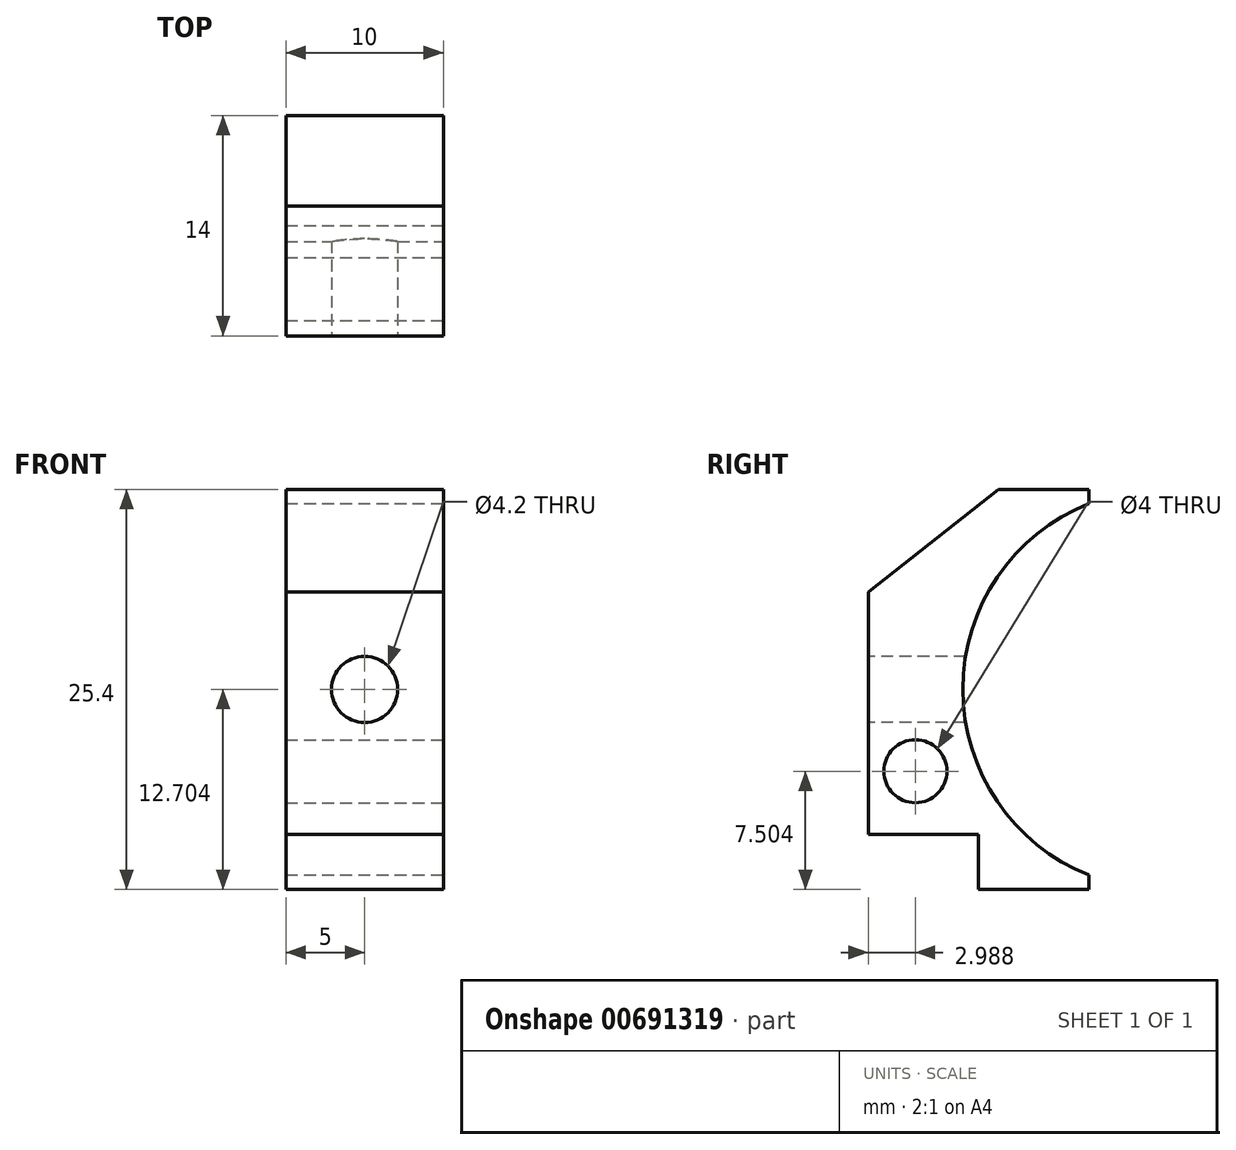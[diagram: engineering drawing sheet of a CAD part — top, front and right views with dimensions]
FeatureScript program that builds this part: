
annotation { "Feature Type Name" : "Feature", "Feature Type Description" : "" }
export const myFeature = defineFeature(function(context is Context, id is Id, definition is map)
    precondition{}
    {
        {
            var Q0;
            Q0=qCreatedBy(makeId("Front.planeOp"),FACE);
            var sketch = newSketch(context, id + "F0", { "sketchPlane" : qUnion([Q0])});
            skLineSegment(sketch, "E0.top", {"start": v(0, 21.04) * mm, "end": v(10, 21.04) * mm});
            skLineSegment(sketch, "E0.left", {"start": v(0, 0) * mm, "end": v(0, 21.04) * mm});
            skLineSegment(sketch, "E0.right", {"start": v(10, 0) * mm, "end": v(10, 21.04) * mm});
            skLineSegment(sketch, "E1.top", {"start": v(10, -4.36) * mm, "end": v(0, -4.36) * mm});
            skLineSegment(sketch, "E1.left", {"start": v(10, 0) * mm, "end": v(10, -4.36) * mm});
            skLineSegment(sketch, "E1.right", {"start": v(0, 0) * mm, "end": v(0, -4.36) * mm});
            skSolve(sketch);
        }
        {
            var Q0;
            Q0 = qSketchRegion(id + "F0", true);
            extrude(context, id + "F1", {"entities" : qUnion([Q0]), "depth" : 14 * mm, "offsetDistance" : 25.4 * mm});
        }
        {
            var Q0;
            Q0=makeQuery(id+"F1.opExtrude","SWEPT_FACE",FACE,{"disambiguationData":[OSD([sQuery(id+"F0.wireOp",EDGE,"E0.right")])]});
            var sketch = newSketch(context, id + "F2", { "sketchPlane" : qUnion([Q0])});
            skLineSegment(sketch, "E2", {"start": v(1.53, 21.04) * mm, "end": v(24.73, 21.04) * mm, "construction": true});
            skLineSegment(sketch, "E3.bottom", {"start": v(1.53, 21.04) * mm, "end": v(7.88, 21.04) * mm});
            skLineSegment(sketch, "E3.top", {"start": v(2.6, -4.36) * mm, "end": v(8.96, -4.36) * mm});
            skPoint(sketch, "E4.centerSnap0", {"position": v(1.53, 8.34) * mm});
            skPoint(sketch, "E4.centerSnap1", {"position": v(4.7, 21.04) * mm});
            skLineSegment(sketch, "E5", {"start": v(0, -4.36) * mm, "end": v(0, 21.04) * mm});
            skPoint(sketch, "E6", {"position": v(7.88, 8.34) * mm});
            skLineSegment(sketch, "E7", {"start": v(-14, 8.34) * mm, "end": v(-8.02, 8.34) * mm, "construction": true});
            skLineSegment(sketch, "E8", {"start": v(4.7, 21.04) * mm, "end": v(4.7, 8.34) * mm});
            skLineSegment(sketch, "E9", {"start": v(1.53, 8.34) * mm, "end": v(7.88, 8.34) * mm, "construction": true});
            skLineSegment(sketch, "E10.bottom", {"start": v(1.53, 21.04) * mm, "end": v(7.87, 21.04) * mm});
            skLineSegment(sketch, "E10.top", {"start": v(1.53, -4.36) * mm, "end": v(7.87, -4.36) * mm});
            skLineSegment(sketch, "E10.left", {"start": v(1.53, 21.04) * mm, "end": v(1.53, -4.36) * mm});
            skLineSegment(sketch, "E10.right", {"start": v(7.87, 21.04) * mm, "end": v(7.87, -4.36) * mm});
            skPoint(sketch, "E10.middle", {"position": v(4.7, 8.34) * mm});
            skArc(sketch, "E11", {"start": v(1.52, 21.04) * mm, "mid": v(-2.07, 19.55) * mm, "end": v(-5.07, 17.06) * mm, "construction": true});
            skLineSegment(sketch, "E12", {"start": v(4.7, 8.34) * mm, "end": v(0, 20.56) * mm, "construction": true});
            skLineSegment(sketch, "E13", {"start": v(4.7, 8.34) * mm, "end": v(1.52, 21.04) * mm, "construction": true});
            skArc(sketch, "E14", {"start": v(4.7, 21.04) * mm, "mid": v(-8, 8.34) * mm, "end": v(4.7, -4.36) * mm});
            skLineSegment(sketch, "E15", {"start": v(-7, -4.36) * mm, "end": v(0, -4.36) * mm});
            skLineSegment(sketch, "E16", {"start": v(-7, -4.36) * mm, "end": v(-7, -0.86) * mm});
            skLineSegment(sketch, "E17", {"start": v(-7, -0.86) * mm, "end": v(-14, -0.86) * mm});
            skLineSegment(sketch, "E18", {"start": v(-14, -0.86) * mm, "end": v(-14, 8.34) * mm});
            skLineSegment(sketch, "E19", {"start": v(-38, -0.86) * mm, "end": v(-14, -0.86) * mm, "construction": true});
            skLineSegment(sketch, "E20", {"start": v(-34.79, -0.86) * mm, "end": v(-34.79, 3.14) * mm, "construction": true});
            skPoint(sketch, "E21.centerSnap0", {"position": v(-11.01, 8.34) * mm});
            skCircle(sketch, "E22", {"center": v(-11.01, 3.14) * mm, "radius": 2 * mm});
            skSolve(sketch);
        }
        {
            var Q0;
            {var subQ0=sQuery(id+"F2.wireOp",EDGE,"E5");var subQ3=sQuery(id+"F2.wireOp",EDGE,"THwo0RVz-D03a-z8GB-oCDg-kRwS6JTPJZCc");var subQ5=makeQuery(id+"F2.imprint","INTERSECT",VERTEX,{"derivedFrom":[subQ0,subQ3]});Q0=makeQuery(id+"F2.imprint","IMPRINT",FACE,{"disambiguationData":[TD([[makeQuery(id+"F2.imprint","IMPRINT",EDGE,{"disambiguationData":[TD([[subQ5,1.0]])],"derivedFrom":subQ3}),1.0]])]});}
            var Q1;
            {var subQ2=sQuery(id+"F2.wireOp",EDGE,"pF1QTI6O-Y2cm-lT8T-25oJ-yhtP9O5BMF4k");Q1=makeQuery(id+"F2.imprint","IMPRINT",FACE,{"disambiguationData":[TD([[makeQuery(id+"F2.imprint","IMPRINT",EDGE,{"derivedFrom":subQ2}),-1.0]])]});}
            var Q2;
            {var subQ0=sQuery(id+"F2.wireOp",EDGE,"E5");var subQ3=sQuery(id+"F2.wireOp",EDGE,"E14");var subQ5=makeQuery(id+"F2.imprint","INTERSECT",VERTEX,{"derivedFrom":[subQ0,subQ3]});Q2=makeQuery(id+"F2.imprint","IMPRINT",FACE,{"disambiguationData":[TD([[makeQuery(id+"F2.imprint","IMPRINT",EDGE,{"disambiguationData":[TD([[subQ5,1.0]])],"derivedFrom":subQ3}),1.0]])]});}
            var Q3;
            {var subQ0=sQuery(id+"F2.wireOp",EDGE,"7ex8zuft-uerx-yqms-d6Cl-iXTFEyRzaDfW.bottom");var subQ3=sQuery(id+"F2.wireOp",EDGE,"E14");var subQ4=makeQuery(id+"F2.imprint","INTERSECT",VERTEX,{"derivedFrom":[subQ0,subQ3]});Q3=makeQuery(id+"F2.imprint","IMPRINT",FACE,{"disambiguationData":[TD([[makeQuery(id+"F2.imprint","IMPRINT",EDGE,{"disambiguationData":[TD([[subQ4,1.0]])],"derivedFrom":subQ3}),1.0]])]});}
            var Q4;
            {var subQ0=sQuery(id+"F2.wireOp",EDGE,"N75xu5ub-JoDY-6aet-Vx7b-B6GqsqUpSeAX");Q4=makeQuery(id+"F2.imprint","IMPRINT",FACE,{"disambiguationData":[TD([[makeQuery(id+"F2.imprint","IMPRINT",EDGE,{"derivedFrom":subQ0}),1.0]])]});}
            extrude(context, id + "F3", {"entities" : qUnion([Q0, Q1, Q2, Q3, Q4]), "operationType" : NewBodyOperationType.ADD, "oppositeDirection" : true, "depth" : 11 * mm, "offsetDistance" : 25.4 * mm});
        }
        {
            var Q0;
            Q0=makeQuery(id+"F1.opExtrude","CAP_FACE",FACE,{"disambiguationData":[OSD([sQuery(id+"F0.wireOp",EDGE,"E0.bottom"),sQuery(id+"F0.wireOp",EDGE,"E0.top"),sQuery(id+"F0.wireOp",EDGE,"E0.left"),sQuery(id+"F0.wireOp",EDGE,"E0.right")])],"isStart":false});
            var sketch = newSketch(context, id + "F4", { "sketchPlane" : qUnion([Q0])});
            skLineSegment(sketch, "E23", {"start": v(-7.1, 21.04) * mm, "end": v(-7.1, 8.34) * mm, "construction": true});
            skCircle(sketch, "E24", {"center": v(5, 8.34) * mm, "radius": 2.1 * mm});
            skPoint(sketch, "E24.centerSnap0", {"position": v(5, 21.04) * mm});
            skSolve(sketch);
        }
        {
            var Q0;
            Q0=makeQuery(id+"F4.imprint","IMPRINT",FACE,{"disambiguationData":[TD([[makeQuery(id+"F4.imprint","IMPRINT",EDGE,{"derivedFrom":sQuery(id+"F4.wireOp",EDGE,"E24")}),1.0]])]});
            extrude(context, id + "F5", {"entities" : qUnion([Q0]), "operationType" : NewBodyOperationType.REMOVE, "endBound" : BoundingType.THROUGH_ALL, "oppositeDirection" : true, "depth" : 25.4 * mm, "offsetDistance" : 25.4 * mm});
        }
        {
            var Q0;
            Q0=makeQuery(id+"F1.opExtrude","CAP_EDGE",EDGE,{"disambiguationData":[OSD([sQuery(id+"F0.wireOp",EDGE,"E0.top")])],"isStart":false});
            chamfer(context, id + "F6", {"entities" : qUnion([Q0]), "chamferType" : ChamferType.TWO_OFFSETS, "width1" : 8.25 * mm, "oppositeDirection" : false, "width2" : 6.5 * mm, "tangentPropagation" : true});
        }
        {
            var Q0;
            {var subQ0=sQuery(id+"F2.wireOp",EDGE,"7ex8zuft-uerx-yqms-d6Cl-iXTFEyRzaDfW.bottom");var subQ3=sQuery(id+"F2.wireOp",EDGE,"E14");var subQ4=makeQuery(id+"F2.imprint","INTERSECT",VERTEX,{"derivedFrom":[subQ0,subQ3]});Q0=makeQuery(id+"F2.imprint","IMPRINT",FACE,{"disambiguationData":[TD([[makeQuery(id+"F2.imprint","IMPRINT",EDGE,{"disambiguationData":[TD([[subQ4,1.0]])],"derivedFrom":subQ3}),1.0]])]});}
            var Q1;
            {var subQ0=sQuery(id+"F2.wireOp",EDGE,"E5");var subQ3=sQuery(id+"F2.wireOp",EDGE,"E14");var subQ5=makeQuery(id+"F2.imprint","INTERSECT",VERTEX,{"derivedFrom":[subQ0,subQ3]});Q1=makeQuery(id+"F2.imprint","IMPRINT",FACE,{"disambiguationData":[TD([[makeQuery(id+"F2.imprint","IMPRINT",EDGE,{"disambiguationData":[TD([[subQ5,1.0]])],"derivedFrom":subQ3}),1.0]])]});}
            extrude(context, id + "F7", {"entities" : qUnion([Q0, Q1]), "operationType" : NewBodyOperationType.REMOVE, "oppositeDirection" : true, "depth" : 25.4 * mm, "offsetDistance" : 25.4 * mm});
        }
        {
            var Q0;
            {var subQ0=sQuery(id+"F2.wireOp",EDGE,"E16");Q0=makeQuery(id+"F2.imprint","IMPRINT",FACE,{"disambiguationData":[TD([[makeQuery(id+"F2.imprint","IMPRINT",EDGE,{"derivedFrom":subQ0}),1.0]])]});}
            extrude(context, id + "F8", {"entities" : qUnion([Q0]), "operationType" : NewBodyOperationType.REMOVE, "endBound" : BoundingType.THROUGH_ALL, "oppositeDirection" : true, "depth" : 25 * mm, "offsetDistance" : 25 * mm});
        }
        {
            var Q0;
            Q0 = qSketchRegion(id + "F2", true);
            extrude(context, id + "F9", {"entities" : qUnion([Q0]), "operationType" : NewBodyOperationType.REMOVE, "oppositeDirection" : true, "depth" : 25 * mm, "offsetDistance" : 25 * mm});
        }
    });
